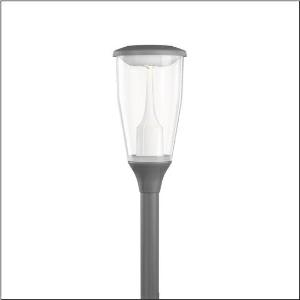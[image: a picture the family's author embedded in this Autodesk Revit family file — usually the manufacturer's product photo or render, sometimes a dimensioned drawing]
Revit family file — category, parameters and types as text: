
# Revit family: dl_11_iq___p1_0a_5xa5575nf14hp00022_d0ce
name_source: partatom
category: Lighting Fixtures
units: mm (PartAtom-declared; Revit-internal decimal feet)

## family parameters
Cut with Voids When Loaded = No
Host = Face
Light Source = No
Part Type = Normal
Room Calculation Point = No
Round Connector Dimension = Use Diameter
Shared = No

## types (1)
- --- (1 x LED, 4280 lm, 33.6 W, 2700K)
    Apparent Load = 34 VA
    CIE Flux Codes = 23 60 93 95 100
    Color Rendering = 70
    Color Temperature = 2700K
    Default Elevation = 1800 mm
    Description = DL 11 iQ, mast luminaire, Module 540 iQ-SR, primary light control with 3 zone facetted reflector, of plastic, silver coated, highly specular, structured, primary optical cover: cover, of PMMA, transparent, light distribution: P1.0a, light emission: direct distribution, primary light characteristic: asymmetric, installation type: post-top, LED, High Power LED, light colour: 727, colour temperature: 2700K, control: Street-Remote, Auto-Match, Temp-Guard, Lumen-Switch, Night-Set, Smart-Wire, Light-Fading, Desk-Remote (wireless, voltage-free reading and setting of iQ features in the workshop via application-optimized NFC function/RFID function), optimised constant luminous flux control (CLO 2.0), mains connection: 220..240V, AC, 50/60Hz, connection cable pre-assembled, cable length: 5,5m, wiring characteristics: H07RN-F, 5-core, 1.5mm², start of lifetime: 34W, end of service life: 36W, luminaire housing, upper part, of diecast aluminium, coated, Siteco® metallic grey (DB 702S), spigot size: 76mm (post-top), post-top mast mounting element, of diecast aluminium, coated, Siteco® metallic grey (DB 702S), Module 540 iQ-SR, traffic white (RAL 9016), equipment: Power, protection rating (complete): IP66, insulation class (complete): insulation class II (safety insulation), certification: CE, ENEC, ENEC+, VDE, packaging unit: 1 piece

Light Distribution: P1.0a
    Height = 665 mm
    Lamp = 1 x LED
    Lamp Light Flux = 4280 lm
    Lamp Power = 33.6 W
    Lamp count = 1
    Length = 334 mm
    Luminous efficacy = 127 lm/W
    Manufacturer = Siteco
    ModVariant = No
    Model = 5XA5575NF14HP00022
    Number of Poles = 1
    OnlyDefault = Yes
    Power Factor = 1
    Product Name = DL 11 iQ | P1.0a
    Product group = mast luminaire | pylon top
    ProductGroupID = 6100
    Protection Class = Protection class II
    Protection Degree = IP 66
    RLX_Detail_Level = 1
    RLX_Emergency_Light_Flux = 0 lm
    RLX_Emergency_Type = 0
    RLX_Emergency_Type_DB = No
    RlxData = <blob elided: 103925 chars, md5=5795061f>
    Socket = socket
    Standby Power = 0 W
    System Light Flux = 4280 lm
    System Power = 34 W
    Type Comments = factory setting: luminous flux: 100 % | dim-lin: 254 | 695 mA
    Type Image = l_1258354.jpg
    URL = http://relux.com
    VarID = @adj_021745
    Voltage = 0 V
    Weight = 0.00 kg
    Width = 0 mm  [stored 0 ft]

note: [stored X ft] marks values corroborated as IEEE doubles in the binary element streams (Revit-internal decimal feet)

## geometry (parser evidence)
native form markers: Blend x4, Sweep x11
no freeform markers — native parametric forms only
